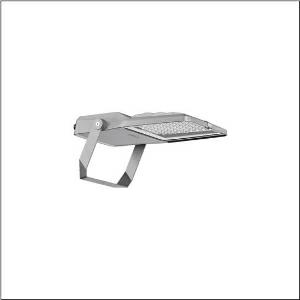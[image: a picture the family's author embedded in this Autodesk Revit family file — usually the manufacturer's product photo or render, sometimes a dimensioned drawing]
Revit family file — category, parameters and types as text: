
# Revit family: floodlight_fl_21_mini___pl33t_5xa7776d2f1a_88fb
name_source: partatom
category: Lighting Fixtures
units: mm (PartAtom-declared; Revit-internal decimal feet)

## family parameters
Cut with Voids When Loaded = No
Host = Face
Light Source = No
Part Type = Normal
Room Calculation Point = No
Round Connector Dimension = Use Diameter
Shared = No

## types (1)
- --- (1 x LED, 17630 lm, 142.9 W, 3000K)
    Apparent Load = 143 VA
    CIE Flux Codes = 26 75 99 100 100
    Color Rendering = 70
    Color Temperature = 3000K
    Default Elevation = 1800 mm
    Description = Floodlight FL 21 mini, floodlight, primary light control with lens, of PMMA, primary optical cover: protective disc, of toughened safety glass, transparent, light distribution: PL33T, light emission: direct distribution, installation type: surface-mounted, LED, High Power LED, rated luminous flux: 17.630lm, luminous efficacy: 123lm/W, light colour: 730, colour temperature: 3000K, control gear: Smart Interface (Zhaga), control: flexible luminous flux parameterisation, time-dependent luminous flux control, constant luminous flux control, overheat protection, pre-setting: logarithmic dimming characteristic, with terminal, 6-pole, mains connection: 220..240V, AC, 50/60Hz, start of lifetime: 143W, end of service life: 151W, reduction: 63W, luminaire housing, of diecast aluminium, powder-coated, SITECO metallic grey (DB 702S), corrosivity category C5 mid according to DIN EN ISO 12944, suitable for swimming pools, chlorine-resistant, sealing non-destructively replaceable, mounting bracket, of steel, galvanised, powder-coated, SITECO metallic grey (DB 702S), Smart Interface below and above, protection rating (complete): IP66, insulation class (complete): insulation class II (safety insulation), certification: CE, ENEC, VDE, protection symbol: D, impact resistance: IK08, permissible operating ambient temperature: -40..+40°C, permissible operating ambient temperature for outdoor applications: -40..+50°C, standard: DIN EN 12944, LABS conformity tested according to VDMA 24364:2018-05, packaging unit: 1 piece

Light Distribution: PL33T
    Height = 70 mm
    Lamp = 1 x LED
    Lamp Light Flux = 17630 lm
    Lamp Power = 142.9 W
    Lamp count = 1
    Length = 485 mm
    Luminous efficacy = 123 lm/W
    Manufacturer = Siteco
    ModVariant = No
    Model = 5XA7776D2F1A
    Number of Poles = 1
    OnlyDefault = Yes
    Power Factor = 1
    Product Name = Floodlight FL 21 mini | PL33T
    Product group = floodlight | pylon annexe
    ProductGroupID = 6201
    Protection Class = Protection class II
    Protection Degree = IP 66
    RLX_Detail_Level = 1
    RLX_Emergency_Light_Flux = 0 lm
    RLX_Emergency_Type = 0
    RLX_Emergency_Type_DB = No
    RlxData = <blob elided: 96233 chars, md5=4442c978>
    Socket = socket
    Standby Power = 0 W
    System Light Flux = 17630 lm
    System Power = 143 W
    Type Comments = factory setting: luminous flux: 100 % | dim-lin: 254 | 730 mA
    Type Image = l_1006845.jpg
    URL = http://relux.com
    VarID = @adj_147857
    Voltage = 0 V
    Weight = 0.00 kg
    Width = 337 mm

## geometry (parser evidence)
native form markers: Blend x4, Sweep x10
no freeform markers — native parametric forms only
